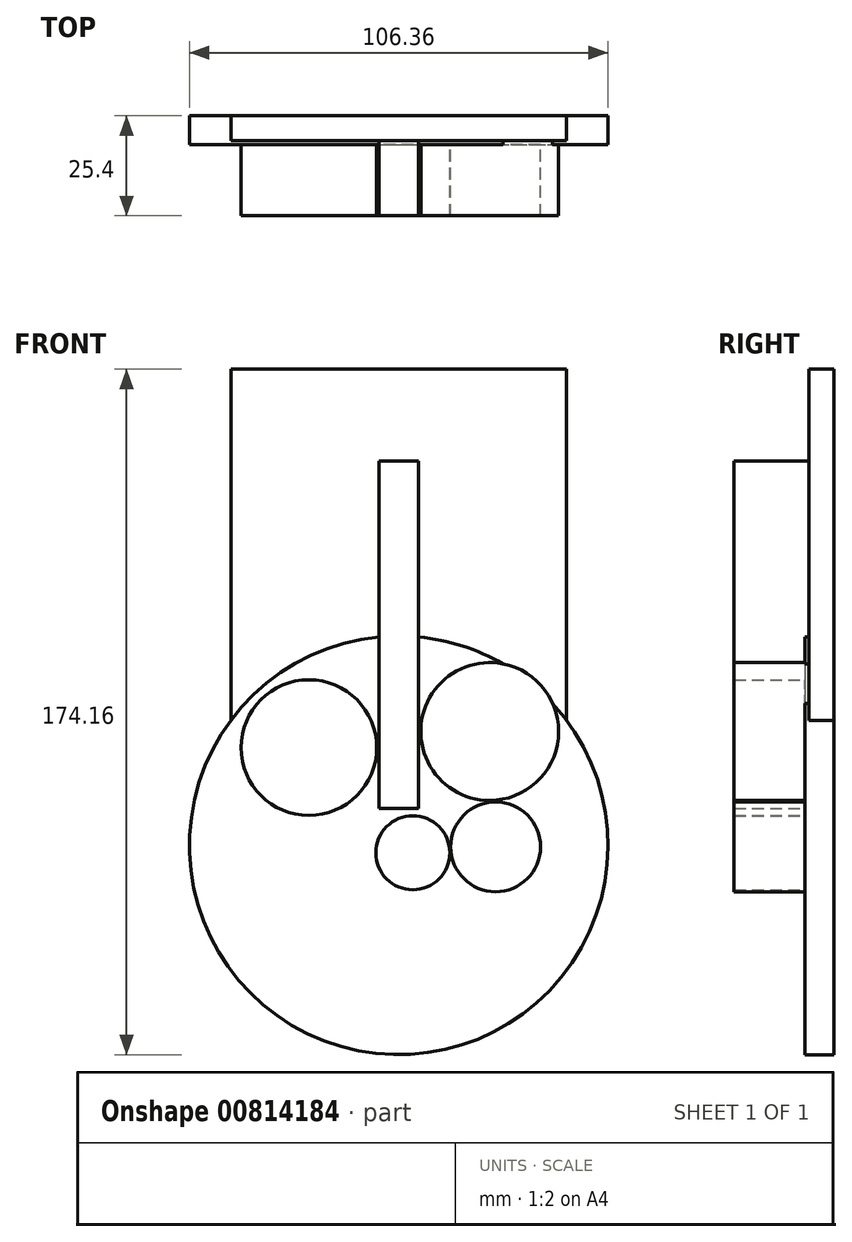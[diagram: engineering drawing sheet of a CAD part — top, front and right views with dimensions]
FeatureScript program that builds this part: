
annotation { "Feature Type Name" : "Feature", "Feature Type Description" : "" }
export const myFeature = defineFeature(function(context is Context, id is Id, definition is map)
    precondition{}
    {
        {
            var Q0;
            Q0=qCreatedBy(makeId("Front.planeOp"),FACE);
            var sketch = newSketch(context, id + "F0", { "sketchPlane" : qUnion([Q0])});
            skLineSegment(sketch, "E0.bottom", {"start": v(42.64, -67.44) * mm, "end": v(-42.64, -67.44) * mm});
            skLineSegment(sketch, "E0.top", {"start": v(42.64, 67.44) * mm, "end": v(-42.64, 67.44) * mm});
            skLineSegment(sketch, "E0.left", {"start": v(42.64, -67.44) * mm, "end": v(42.64, 67.44) * mm});
            skLineSegment(sketch, "E0.right", {"start": v(-42.64, -67.44) * mm, "end": v(-42.64, 67.44) * mm});
            skPoint(sketch, "E0.middle", {"position": v(0, 0) * mm});
            skSolve(sketch);
        }
        {
            var Q0;
            Q0=qCreatedBy(makeId("Front.planeOp"),FACE);
            var sketch = newSketch(context, id + "F1", { "sketchPlane" : qUnion([Q0])});
            skLineSegment(sketch, "E1.bottom", {"start": v(5.07, -44.14) * mm, "end": v(-5.07, -44.14) * mm});
            skLineSegment(sketch, "E1.top", {"start": v(5.07, 44.14) * mm, "end": v(-5.07, 44.14) * mm});
            skLineSegment(sketch, "E1.left", {"start": v(5.07, -44.14) * mm, "end": v(5.07, 44.14) * mm});
            skLineSegment(sketch, "E1.right", {"start": v(-5.07, -44.14) * mm, "end": v(-5.07, 44.14) * mm});
            skPoint(sketch, "E1.middle", {"position": v(0, 0) * mm});
            skSolve(sketch);
        }
        {
            var Q0;
            Q0=qCreatedBy(makeId("Front.planeOp"),FACE);
            var sketch = newSketch(context, id + "F2", { "sketchPlane" : qUnion([Q0])});
            skCircle(sketch, "E2", {"center": v(23.1, -24.6) * mm, "radius": 17.51 * mm});
            skCircle(sketch, "E3", {"center": v(-22.84, -28.72) * mm, "radius": 17.24 * mm});
            skCircle(sketch, "E4", {"center": v(24.6, -53.91) * mm, "radius": 11.4 * mm});
            skSolve(sketch);
        }
        {
            var Q0;
            Q0=qCreatedBy(makeId("Front.planeOp"),FACE);
            var sketch = newSketch(context, id + "F3", { "sketchPlane" : qUnion([Q0])});
            skCircle(sketch, "E5", {"center": v(3.57, -55.42) * mm, "radius": 9.4 * mm});
            skSolve(sketch);
        }
        {
            var Q0;
            Q0=qCreatedBy(makeId("Front.planeOp"),FACE);
            var sketch = newSketch(context, id + "F4", { "sketchPlane" : qUnion([Q0])});
            skCircle(sketch, "E6", {"center": v(0, -53.54) * mm, "radius": 53.18 * mm});
            skSolve(sketch);
        }
        {
            var Q0;
            Q0=makeQuery(id+"F4.imprint","IMPRINT",FACE,{"disambiguationData":[TD([[makeQuery(id+"F4.imprint","IMPRINT",EDGE,{"derivedFrom":sQuery(id+"F4.wireOp",EDGE,"E6")}),1.0]])]});
            extrude(context, id + "F5", {"entities" : qUnion([Q0]), "depth" : 7.37 * mm, "offsetDistance" : 25.4 * mm});
        }
        {
            var Q0;
            Q0 = qSketchRegion(id + "F3", true);
            var Q1;
            Q1 = qSketchRegion(id + "F2", true);
            var Q2;
            Q2 = qSketchRegion(id + "F1", true);
            extrude(context, id + "F6", {"entities" : qUnion([Q0, Q1, Q2]), "operationType" : NewBodyOperationType.ADD, "depth" : 25.4 * mm, "offsetDistance" : 25.4 * mm});
        }
        {
            var Q0;
            Q0=makeQuery(id+"F0.imprint","IMPRINT",FACE,{"disambiguationData":[TD([[makeQuery(id+"F0.imprint","IMPRINT",EDGE,{"derivedFrom":sQuery(id+"F0.wireOp",EDGE,"E0.bottom")}),-1.0]])]});
            extrude(context, id + "F7", {"entities" : qUnion([Q0]), "operationType" : NewBodyOperationType.ADD, "depth" : 6.35 * mm, "offsetDistance" : 25.4 * mm});
        }
    });
